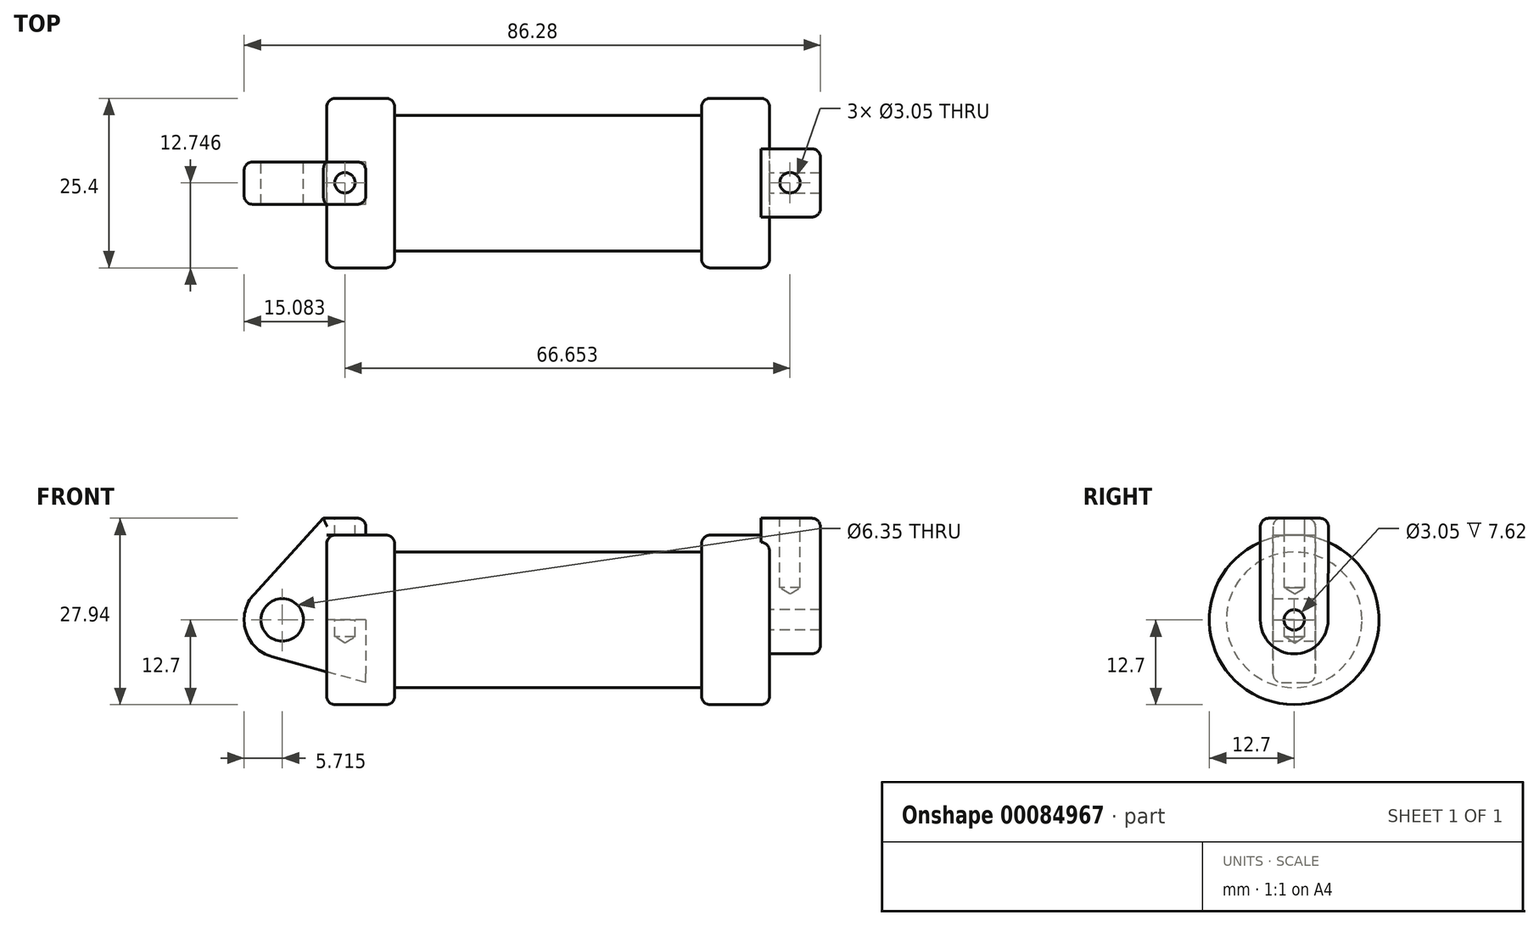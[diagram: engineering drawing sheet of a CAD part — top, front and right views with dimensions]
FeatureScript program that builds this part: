
annotation { "Feature Type Name" : "Feature", "Feature Type Description" : "" }
export const myFeature = defineFeature(function(context is Context, id is Id, definition is map)
    precondition{}
    {
        {
            var Q0;
            Q0=qCreatedBy(makeId("Front.planeOp"),FACE);
            var sketch = newSketch(context, id + "F0", { "sketchPlane" : qUnion([Q0])});
            skLineSegment(sketch, "E0", {"start": v(0, 0) * mm, "end": v(0, 12.7) * mm});
            skLineSegment(sketch, "E1", {"start": v(0, 12.7) * mm, "end": v(10.16, 12.7) * mm});
            skLineSegment(sketch, "E2", {"start": v(10.16, 12.7) * mm, "end": v(10.16, 10.16) * mm});
            skLineSegment(sketch, "E3", {"start": v(10.16, 10.16) * mm, "end": v(56.13, 10.16) * mm});
            skLineSegment(sketch, "E4", {"start": v(56.13, 10.16) * mm, "end": v(56.13, 12.7) * mm});
            skLineSegment(sketch, "E5", {"start": v(56.13, 12.7) * mm, "end": v(66.3, 12.7) * mm});
            skLineSegment(sketch, "E6", {"start": v(66.3, 12.7) * mm, "end": v(66.3, 0) * mm});
            skLineSegment(sketch, "E7", {"start": v(66.3, 0) * mm, "end": v(0, 0) * mm});
            skLineSegment(sketch, "E8", {"start": v(5.84, 15.24) * mm, "end": v(-0.5, 15.24) * mm});
            skLineSegment(sketch, "E9", {"start": v(-0.5, 15.24) * mm, "end": v(-10.88, 3.85) * mm});
            skLineSegment(sketch, "E10", {"start": v(0, 0) * mm, "end": v(-6.65, 0) * mm});
            skCircle(sketch, "E11", {"center": v(-6.65, 0) * mm, "radius": 5.72 * mm});
            skCircle(sketch, "E12", {"center": v(-6.65, 0) * mm, "radius": 3.18 * mm});
            skLineSegment(sketch, "E13", {"start": v(5.84, 15.24) * mm, "end": v(5.84, -9.4) * mm});
            skLineSegment(sketch, "E14", {"start": v(5.84, -9.4) * mm, "end": v(-8.18, -5.5) * mm});
            skSolve(sketch);
        }
        {
            var Q0;
            {var subQ0=sQuery(id+"F0.wireOp",EDGE,"E0");Q0=makeQuery(id+"F0.imprint","IMPRINT",FACE,{"disambiguationData":[TD([[makeQuery(id+"F0.imprint","IMPRINT",EDGE,{"derivedFrom":subQ0}),-1.0]])]});}
            var Q1;
            {var subQ0=sQuery(id+"F0.wireOp",EDGE,"E2");Q1=makeQuery(id+"F0.imprint","IMPRINT",FACE,{"disambiguationData":[TD([[makeQuery(id+"F0.imprint","IMPRINT",EDGE,{"derivedFrom":subQ0}),-1.0]])]});}
            var Q2;
            Q2=sQuery(id+"F0.wireOp",EDGE,"E7");
            revolve(context, id + "F1", {"entities" : qUnion([Q0, Q1]), "axis" : qUnion([Q2]), "revolveType" : RevolveType.FULL});
        }
        {
            var Q0;
            {var subQ0=sQuery(id+"F0.wireOp",EDGE,"E14");Q0=makeQuery(id+"F0.imprint","IMPRINT",FACE,{"disambiguationData":[TD([[makeQuery(id+"F0.imprint","IMPRINT",EDGE,{"derivedFrom":subQ0}),-1.0]])]});}
            var Q1;
            {var subQ3=sQuery(id+"F0.wireOp",EDGE,"E0");Q1=makeQuery(id+"F0.imprint","IMPRINT",FACE,{"disambiguationData":[TD([[makeQuery(id+"F0.imprint","IMPRINT",EDGE,{"derivedFrom":subQ3}),1.0]])]});}
            var Q2;
            {var subQ4=sQuery(id+"F0.wireOp",EDGE,"E12");Q2=makeQuery(id+"F0.imprint","IMPRINT",FACE,{"disambiguationData":[TD([[makeQuery(id+"F0.imprint","IMPRINT",EDGE,{"derivedFrom":subQ4}),-1.0]])]});}
            var Q3;
            Q3=sQuery(id+"F0.wireOp",EDGE,"E8");
            var Q4;
            Q4=sQuery(id+"F0.wireOp",EDGE,"E13");
            var Q5;
            Q5=sQuery(id+"F0.wireOp",EDGE,"E14");
            var Q6;
            Q6=sQuery(id+"F0.wireOp",EDGE,"E11");
            var Q7;
            Q7=sQuery(id+"F0.wireOp",EDGE,"E12");
            var Q8;
            Q8=sQuery(id+"F0.wireOp",EDGE,"E9");
            extrude(context, id + "F2", {"entities" : qUnion([Q0, Q1, Q2]), "surfaceEntities" : qUnion([Q3, Q4, Q5, Q6, Q7, Q8]), "endBound" : BoundingType.SYMMETRIC, "depth" : 6.35 * mm});
        }
        {
            var Q0;
            Q0=makeQuery(id+"F1.opRevolve","SWEPT_FACE",FACE,{"disambiguationData":[OSD([sQuery(id+"F0.wireOp",EDGE,"E6")])]});
            var sketch = newSketch(context, id + "F3", { "sketchPlane" : qUnion([Q0])});
            skCircle(sketch, "E15", {"center": v(0, 0) * mm, "radius": 5.08 * mm});
            skCircle(sketch, "E16", {"center": v(0, 0) * mm, "radius": 1.52 * mm});
            skLineSegment(sketch, "E17", {"start": v(-5.08, 0) * mm, "end": v(-5.08, 15.22) * mm});
            skLineSegment(sketch, "E18", {"start": v(-5.08, 15.22) * mm, "end": v(5.14, 15.22) * mm});
            skLineSegment(sketch, "E19", {"start": v(5.14, 15.22) * mm, "end": v(5.08, -0.02) * mm});
            skSolve(sketch);
        }
        {
            var Q0;
            Q0=qSketchRegion(id+"F3",true);
            extrude(context, id + "F4", {"entities" : qUnion([Q0]), "operationType" : NewBodyOperationType.ADD, "depth" : 7.62 * mm});
        }
        {
            var Q0;
            Q0=makeQuery(id+"F4.opExtrude","CAP_FACE",FACE,{"disambiguationData":[OSD([sQuery(id+"F3.wireOp",EDGE,"E15"),sQuery(id+"F3.wireOp",EDGE,"E16"),sQuery(id+"F3.wireOp",EDGE,"E17"),sQuery(id+"F3.wireOp",EDGE,"E18"),sQuery(id+"F3.wireOp",EDGE,"E19")])],"isStart":true});
            extrude(context, id + "F5", {"entities" : qUnion([Q0]), "operationType" : NewBodyOperationType.ADD, "depth" : 1.27 * mm});
        }
        {
            var Q0;
            {var subQ0=sQuery(id+"F3.wireOp",EDGE,"E18");Q0=makeQuery(id+"F5.boolean.opBoolean","MERGE",FACE,{"derivedFrom":[makeQuery(id+"F4.opExtrude","SWEPT_FACE",FACE,{"disambiguationData":[OSD([subQ0])]}),makeQuery(id+"F5.opExtrude","SWEPT_FACE",FACE,{"disambiguationData":[OSD([subQ0])]})]});}
            var sketch = newSketch(context, id + "F6", { "sketchPlane" : qUnion([Q0])});
            skCircle(sketch, "E20", {"center": v(69.37, 0.05) * mm, "radius": 1.52 * mm});
            skSolve(sketch);
        }
        {
            var Q0;
            Q0=sQuery(id+"F6.wireOp",VERTEX,"E20.center");
            var Q1;
            Q1=makeQuery(id+"F1.opRevolve","SWEPT_BODY",BODY,{"disambiguationData":[OSD([sQuery(id+"F0.wireOp",EDGE,"E0"),sQuery(id+"F0.wireOp",EDGE,"E1"),sQuery(id+"F0.wireOp",EDGE,"E2"),sQuery(id+"F0.wireOp",EDGE,"E3"),sQuery(id+"F0.wireOp",EDGE,"E4"),sQuery(id+"F0.wireOp",EDGE,"E5"),sQuery(id+"F0.wireOp",EDGE,"E6"),sQuery(id+"F0.wireOp",EDGE,"E7")])]});
            hole(context, id + "F7", {"style" : HoleStyle.SIMPLE, "endStyle" : HoleEndStyle.BLIND, "holeDiameter" : 3.05 * mm, "holeDepth" : 10.4 * mm, "locations" : qUnion([Q0]), "scope" : qUnion([Q1])});
        }
        {
            var Q0;
            Q0=makeQuery(id+"F2.opExtrude","SWEPT_FACE",FACE,{"disambiguationData":[OSD([sQuery(id+"F0.wireOp",EDGE,"E8")])]});
            var sketch = newSketch(context, id + "F8", { "sketchPlane" : qUnion([Q0])});
            skCircle(sketch, "E21", {"center": v(2.71, 0.05) * mm, "radius": 1.52 * mm});
            skSolve(sketch);
        }
        {
            var Q0;
            Q0=sQuery(id+"F8.wireOp",VERTEX,"E21.center");
            var Q1;
            Q1=makeQuery(id+"F2.opExtrude","SWEPT_BODY",BODY,{"disambiguationData":[OSD([sQuery(id+"F0.wireOp",EDGE,"E0"),sQuery(id+"F0.wireOp",EDGE,"E1"),sQuery(id+"F0.wireOp",EDGE,"E7"),sQuery(id+"F0.wireOp",EDGE,"E8"),sQuery(id+"F0.wireOp",EDGE,"E9"),sQuery(id+"F0.wireOp",EDGE,"E11"),sQuery(id+"F0.wireOp",EDGE,"E12"),sQuery(id+"F0.wireOp",EDGE,"E13"),sQuery(id+"F0.wireOp",EDGE,"E14")])]});
            hole(context, id + "F9", {"style" : HoleStyle.SIMPLE, "endStyle" : HoleEndStyle.BLIND, "holeDiameter" : 3.05 * mm, "holeDepth" : 17.78 * mm, "locations" : qUnion([Q0]), "scope" : qUnion([Q1])});
        }
        {
            var Q0;
            Q0=makeQuery(id+"F1.opRevolve","SWEPT_EDGE",EDGE,{"disambiguationData":[OSD([sQuery(id+"F0.wireOp",EDGE,"E1"),sQuery(id+"F0.wireOp",EDGE,"E2")])]});
            fillet(context, id + "F10", {"entities" : qUnion([Q0]), "radius" : 1.27 * mm, "tangentPropagation" : true, "allowEdgeOverflow" : false});
        }
        {
            var Q0;
            Q0=makeQuery(id+"F1.opRevolve","SWEPT_EDGE",EDGE,{"disambiguationData":[OSD([sQuery(id+"F0.wireOp",EDGE,"E4"),sQuery(id+"F0.wireOp",EDGE,"E5")])]});
            var Q1;
            Q1=makeQuery(id+"F4.boolean.opBoolean","SPLIT",EDGE,{"disambiguationData":[OD(1.0)],"derivedFrom":makeQuery(id+"F1.opRevolve","SWEPT_EDGE",EDGE,{"disambiguationData":[OSD([sQuery(id+"F0.wireOp",EDGE,"E5"),sQuery(id+"F0.wireOp",EDGE,"E6")])]})});
            var Q2;
            Q2=makeQuery(id+"F1.opRevolve","SWEPT_EDGE",EDGE,{"disambiguationData":[OSD([sQuery(id+"F0.wireOp",EDGE,"E0"),sQuery(id+"F0.wireOp",EDGE,"E1")])]});
            var Q3;
            {var subQ0=sQuery(id+"F0.wireOp",EDGE,"E1");Q3=makeQuery(id+"F10.opFillet","BLEND_EDGE",EDGE,{"blendedFrom":[makeQuery(id+"F1.opRevolve","SWEPT_EDGE",EDGE,{"disambiguationData":[OSD([subQ0,sQuery(id+"F0.wireOp",EDGE,"E2")])]}),makeQuery(id+"F1.opRevolve","SWEPT_FACE",FACE,{"disambiguationData":[OSD([subQ0])]})],"blendedInto":[makeQuery(id+"F1.opRevolve","SWEPT_FACE",FACE,{"disambiguationData":[OSD([subQ0])]})]});}
            var Q4;
            {var subQ0=sQuery(id+"F3.wireOp",EDGE,"E18");var subQ1=sQuery(id+"F3.wireOp",EDGE,"E17");Q4=makeQuery(id+"F5.boolean.opBoolean","MERGE",EDGE,{"derivedFrom":[makeQuery(id+"F4.opExtrude","SWEPT_EDGE",EDGE,{"disambiguationData":[OSD([subQ1,subQ0])]}),makeQuery(id+"F5.opExtrude","SWEPT_EDGE",EDGE,{"disambiguationData":[OSD([subQ1,subQ0])]})]});}
            var Q5;
            Q5=makeQuery(id+"F4.opExtrude","CAP_EDGE",EDGE,{"disambiguationData":[OSD([sQuery(id+"F3.wireOp",EDGE,"E17")])],"isStart":false});
            var Q6;
            Q6=makeQuery(id+"F4.opExtrude","CAP_EDGE",EDGE,{"disambiguationData":[OSD([sQuery(id+"F3.wireOp",EDGE,"E15")])],"isStart":true});
            var Q7;
            {var subQ0=sQuery(id+"F3.wireOp",EDGE,"E17");var subQ1=sQuery(id+"F3.wireOp",EDGE,"E15");Q7=makeQuery(id+"F4.boolean.opBoolean","SPLIT",EDGE,{"disambiguationData":[TD([makeQuery(id+"F4.opExtrude","SWEPT_FACE",FACE,{"disambiguationData":[OSD([subQ1])]})])],"derivedFrom":makeQuery(id+"F4.opExtrude","CAP_EDGE",EDGE,{"disambiguationData":[OSD([subQ0])],"isStart":true})});}
            var Q8;
            Q8=makeQuery(id+"F2.opExtrude","CAP_EDGE",EDGE,{"disambiguationData":[OSD([sQuery(id+"F0.wireOp",EDGE,"E8")])],"isStart":false});
            var Q9;
            Q9=makeQuery(id+"F2.opExtrude","CAP_EDGE",EDGE,{"disambiguationData":[OSD([sQuery(id+"F0.wireOp",EDGE,"E9")])],"isStart":false});
            var Q10;
            Q10=makeQuery(id+"F2.opExtrude","CAP_EDGE",EDGE,{"disambiguationData":[OSD([sQuery(id+"F0.wireOp",EDGE,"E11")])],"isStart":true});
            var Q11;
            Q11=makeQuery(id+"F2.opExtrude","CAP_EDGE",EDGE,{"disambiguationData":[OSD([sQuery(id+"F0.wireOp",EDGE,"E8")])],"isStart":true});
            var Q12;
            {var subQ0=sQuery(id+"F0.wireOp",EDGE,"E13");Q12=makeQuery(id+"F2.opExtrude","CAP_EDGE",EDGE,{"disambiguationData":[OSD([subQ0]),TDD([makeQuery(id+"F0.imprint","IMPRINT",EDGE,{"disambiguationData":[TD([[makeQuery(id+"F0.imprint","INTERSECT",VERTEX,{"derivedFrom":[sQuery(id+"F0.wireOp",EDGE,"E8"),subQ0]}),-1.0]])],"derivedFrom":subQ0})])],"isStart":false});}
            var Q13;
            {var subQ0=sQuery(id+"F0.wireOp",EDGE,"E13");Q13=makeQuery(id+"F2.opExtrude","CAP_EDGE",EDGE,{"disambiguationData":[OSD([subQ0]),TDD([makeQuery(id+"F0.imprint","IMPRINT",EDGE,{"disambiguationData":[TD([[makeQuery(id+"F0.imprint","INTERSECT",VERTEX,{"derivedFrom":[sQuery(id+"F0.wireOp",EDGE,"E8"),subQ0]}),-1.0]])],"derivedFrom":subQ0})])],"isStart":true});}
            var Q14;
            Q14=makeQuery(id+"F4.opExtrude","CAP_EDGE",EDGE,{"disambiguationData":[OSD([sQuery(id+"F3.wireOp",EDGE,"E19")])],"isStart":false});
            var Q15;
            Q15=makeQuery(id+"F4.opExtrude","CAP_EDGE",EDGE,{"disambiguationData":[OSD([sQuery(id+"F3.wireOp",EDGE,"E18")])],"isStart":false});
            var Q16;
            {var subQ0=sQuery(id+"F3.wireOp",EDGE,"E19");var subQ1=sQuery(id+"F3.wireOp",EDGE,"E18");Q16=makeQuery(id+"F5.boolean.opBoolean","MERGE",EDGE,{"derivedFrom":[makeQuery(id+"F4.opExtrude","SWEPT_EDGE",EDGE,{"disambiguationData":[OSD([subQ1,subQ0])]}),makeQuery(id+"F5.opExtrude","SWEPT_EDGE",EDGE,{"disambiguationData":[OSD([subQ1,subQ0])]})]});}
            var Q17;
            Q17=makeQuery(id+"F2.opExtrude","SWEPT_EDGE",EDGE,{"disambiguationData":[OSD([sQuery(id+"F0.wireOp",EDGE,"E8"),sQuery(id+"F0.wireOp",EDGE,"E13")])]});
            fillet(context, id + "F11", {"entities" : qUnion([Q0, Q1, Q2, Q3, Q4, Q5, Q6, Q7, Q8, Q9, Q10, Q11, Q12, Q13, Q14, Q15, Q16, Q17]), "radius" : 1.27 * mm, "tangentPropagation" : true, "allowEdgeOverflow" : false});
        }
    });
